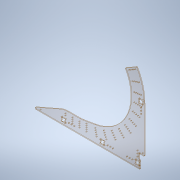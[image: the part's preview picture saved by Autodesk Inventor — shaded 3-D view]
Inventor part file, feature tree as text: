
AUTODESK INVENTOR PART (.ipt)
format: ipt  version: 2020 (Build 240168000, 168)  size: 495,616 bytes
history: native  units: in
note: dims shown in document units (in); Inventor stores cm internally (conversion verified against a paired STEP export)
features: extrude x4, sketch x4, fillet x1
ambient origin geometry x8: Origin, YZ Plane, XZ Plane, XY Plane, X Axis, Y Axis, Z Axis, Center Point
bodies: Solid1 (feature_tree)
feature tree (9):
  extrude  "Extrusion1"  Depth=0.25in
  extrude  "Extrusion2"  Depth=0.25in TaperAngle=0.0deg
  extrude  "Extrusion3"  TaperAngle=0.0deg  [1 undecoded]
  fillet  "Fillet1"  Radius=0.125in
  extrude  "Extrusion4"  Depth=0.5in
  sketch  "Sketch1"  dims[d0=0.25in d1=0.0in d2=0.25in]
  sketch  "Sketch2"  dims[d3=0.5in d4=0.25in d5=0.0in]
  sketch  "Sketch3"  dims[d6=0.3in d7=0.0in d8=0.0in d9=0.125in]
  sketch  "Sketch4"  dims[d10=0.2031in d11=0.5in d12=2.0in d13=0.5in d14=0.5in d15=0.5in d16=0.5in d17=13.134in d18=0.5in d19=0.5in d20=4.7244in d22=120.0deg d24=1.5748in d26=2.0in d27=0.3937in d29=1.0in d31=1.0in d32=0.0in]
note: 1 required parameter value undecoded (feature->parameter linkage not recoverable at this tier; creation-order binding heuristic only, values carry confidence <= 0.55)
